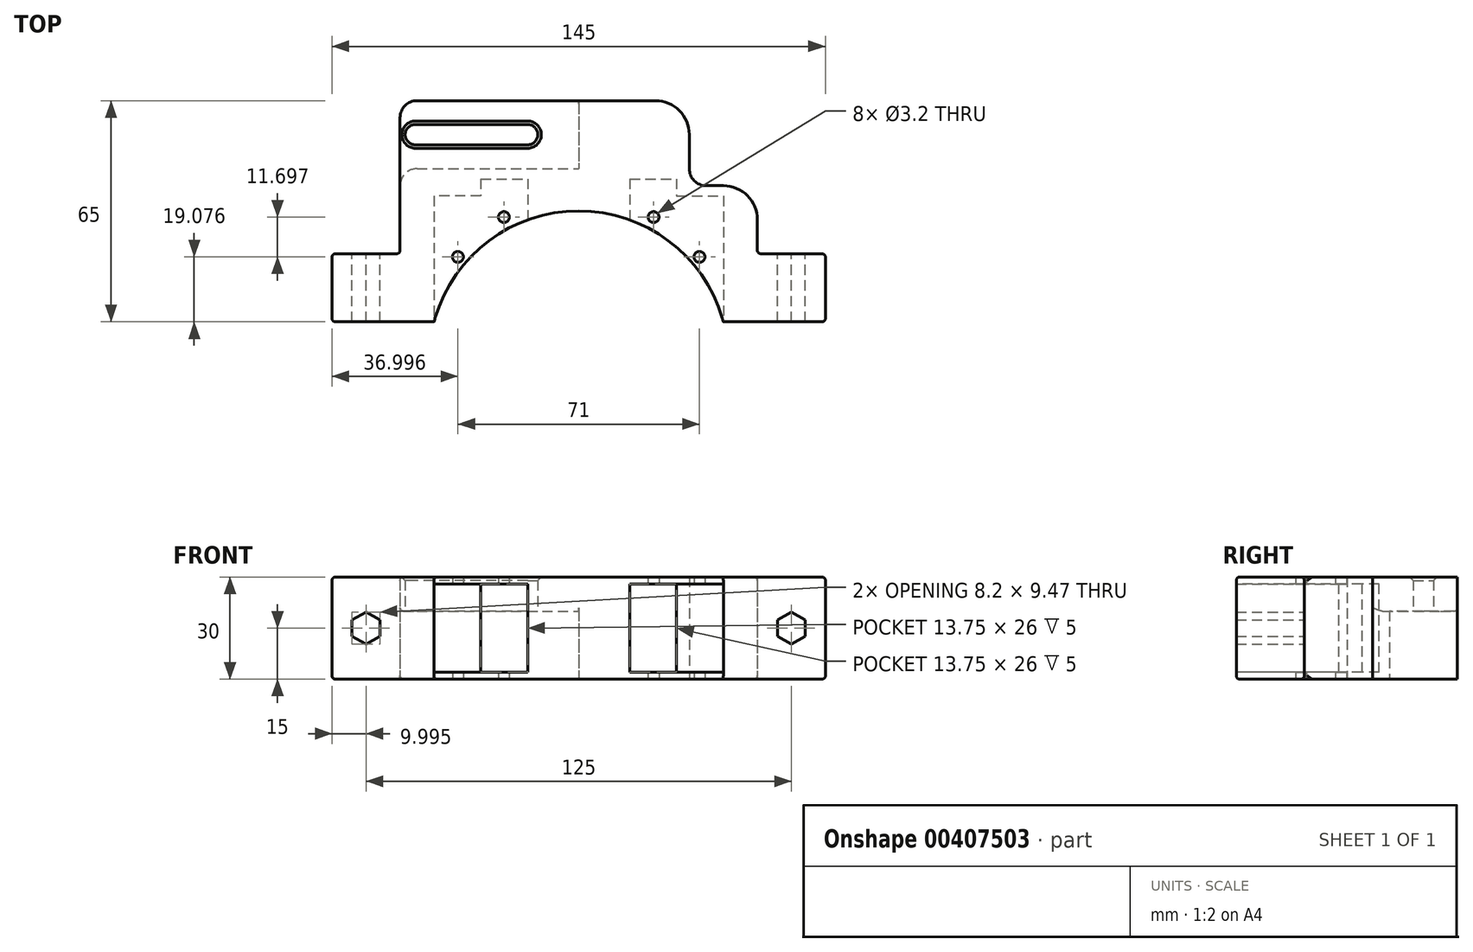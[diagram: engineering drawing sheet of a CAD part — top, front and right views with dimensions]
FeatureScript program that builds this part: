
annotation { "Feature Type Name" : "Feature", "Feature Type Description" : "" }
export const myFeature = defineFeature(function(context is Context, id is Id, definition is map)
    precondition{}
    {
        {
            var Q0;
            Q0=qCreatedBy(makeId("Top.planeOp"),FACE);
            var sketch = newSketch(context, id + "F0", { "sketchPlane" : qUnion([Q0])});
            skLineSegment(sketch, "E0", {"start": v(-52.77, 0.26) * mm, "end": v(-22.77, 0.26) * mm});
            skLineSegment(sketch, "E1", {"start": v(62.23, 0.26) * mm, "end": v(92.23, 0.26) * mm});
            skLineSegment(sketch, "E2", {"start": v(-52.77, 0.26) * mm, "end": v(-52.77, 20.26) * mm});
            skLineSegment(sketch, "E3", {"start": v(-52.77, 20.26) * mm, "end": v(-32.77, 20.26) * mm});
            skLineSegment(sketch, "E4", {"start": v(19.73, -73.35) * mm, "end": v(19.73, 79.15) * mm, "construction": true});
            skPoint(sketch, "E4.endSnap0", {"position": v(19.73, 11.65) * mm});
            skLineSegment(sketch, "E5", {"start": v(92.23, 0.26) * mm, "end": v(92.23, 20.26) * mm});
            skLineSegment(sketch, "E6", {"start": v(92.23, 20.26) * mm, "end": v(72.23, 20.26) * mm});
            skArc(sketch, "E7", {"start": v(62.23, 0.26) * mm, "mid": v(19.73, 32.87) * mm, "end": v(-22.77, 0.26) * mm});
            skLineSegment(sketch, "E8", {"start": v(-32.77, 20.26) * mm, "end": v(-32.77, 40.26) * mm});
            skLineSegment(sketch, "E9", {"start": v(-32.77, 40.26) * mm, "end": v(-12.77, 40.26) * mm});
            skLineSegment(sketch, "E10", {"start": v(-12.77, 40.26) * mm, "end": v(-12.77, 65.26) * mm});
            skLineSegment(sketch, "E11", {"start": v(72.23, 20.26) * mm, "end": v(72.23, 40.26) * mm});
            skLineSegment(sketch, "E12", {"start": v(72.23, 40.26) * mm, "end": v(52.23, 40.26) * mm});
            skLineSegment(sketch, "E13", {"start": v(52.23, 40.26) * mm, "end": v(52.23, 65.26) * mm});
            skLineSegment(sketch, "E14", {"start": v(-12.77, 65.26) * mm, "end": v(52.23, 65.26) * mm});
            skSolve(sketch);
        }
        {
            var Q0;
            Q0=makeQuery(id+"F0.imprint","IMPRINT",FACE,{"disambiguationData":[TD([[makeQuery(id+"F0.imprint","IMPRINT",EDGE,{"derivedFrom":sQuery(id+"F0.wireOp",EDGE,"E0")}),1.0]])]});
            extrude(context, id + "F1", {"entities" : qUnion([Q0]), "depth" : 30 * mm});
        }
        {
            var Q0;
            Q0=makeQuery(id+"F1.opExtrude","SWEPT_FACE",FACE,{"disambiguationData":[OSD([sQuery(id+"F0.wireOp",EDGE,"E0")])]});
            cPlane(context, id + "F2", {"entities" : qUnion([Q0]), "cplaneType" : CPlaneType.OFFSET, "offset" : 0 * mm, "width" : 150 * mm, "height" : 150 * mm});
        }
        {
            var Q0;
            Q0=qCreatedBy(id+"F2.planeOp",FACE);
            var sketch = newSketch(context, id + "F3", { "sketchPlane" : qUnion([Q0])});
            skLineSegment(sketch, "E15", {"start": v(-22.77, 28) * mm, "end": v(4.73, 28) * mm});
            skLineSegment(sketch, "E16", {"start": v(4.73, 28) * mm, "end": v(4.73, 2) * mm});
            skLineSegment(sketch, "E17", {"start": v(4.73, 2) * mm, "end": v(-22.77, 2) * mm});
            skLineSegment(sketch, "E18", {"start": v(-22.77, 2) * mm, "end": v(-22.77, 28) * mm});
            skLineSegment(sketch, "E19", {"start": v(34.73, 28) * mm, "end": v(62.23, 28) * mm});
            skLineSegment(sketch, "E20", {"start": v(62.23, 28) * mm, "end": v(62.23, 2) * mm});
            skLineSegment(sketch, "E21", {"start": v(62.23, 2) * mm, "end": v(34.73, 2) * mm});
            skLineSegment(sketch, "E22", {"start": v(34.73, 2) * mm, "end": v(34.73, 28) * mm});
            skSolve(sketch);
        }
        {
            var Q0;
            Q0=makeQuery(id+"F3.imprint","IMPRINT",FACE,{"disambiguationData":[TD([[makeQuery(id+"F3.imprint","IMPRINT",EDGE,{"derivedFrom":sQuery(id+"F3.wireOp",EDGE,"E15")}),-1.0]])]});
            var Q1;
            Q1=makeQuery(id+"F3.imprint","IMPRINT",FACE,{"disambiguationData":[TD([[makeQuery(id+"F3.imprint","IMPRINT",EDGE,{"derivedFrom":sQuery(id+"F3.wireOp",EDGE,"E19")}),-1.0]])]});
            extrude(context, id + "F4", {"entities" : qUnion([Q0, Q1]), "operationType" : NewBodyOperationType.REMOVE, "oppositeDirection" : true, "depth" : 37 * mm});
        }
        {
            var Q0;
            Q0=makeQuery(id+"F1.opExtrude","SWEPT_FACE",FACE,{"disambiguationData":[OSD([sQuery(id+"F0.wireOp",EDGE,"E3")])]});
            var sketch = newSketch(context, id + "F5", { "sketchPlane" : qUnion([Q0])});
            skCircle(sketch, "E23.cCircle", {"center": v(42.77, 15) * mm, "radius": 4.1 * mm, "construction": true});
            skPoint(sketch, "E23.cCircle.centerSnap0", {"position": v(52.77, 15) * mm});
            skLineSegment(sketch, "E23.0", {"start": v(46.87, 12.63) * mm, "end": v(42.77, 10.27) * mm});
            skLineSegment(sketch, "E23.1", {"start": v(42.77, 10.27) * mm, "end": v(38.67, 12.63) * mm});
            skLineSegment(sketch, "E23.2", {"start": v(38.67, 12.63) * mm, "end": v(38.67, 17.37) * mm});
            skLineSegment(sketch, "E23.3", {"start": v(38.67, 17.37) * mm, "end": v(42.77, 19.73) * mm});
            skLineSegment(sketch, "E23.4", {"start": v(42.77, 19.73) * mm, "end": v(46.87, 17.37) * mm});
            skLineSegment(sketch, "E23.5", {"start": v(46.87, 17.37) * mm, "end": v(46.87, 12.63) * mm});
            skPoint(sketch, "E23.0.midPoint", {"position": v(44.82, 11.45) * mm});
            skSolve(sketch);
        }
        {
            var Q0;
            Q0=makeQuery(id+"F1.opExtrude","SWEPT_FACE",FACE,{"disambiguationData":[OSD([sQuery(id+"F0.wireOp",EDGE,"E6")])]});
            var sketch = newSketch(context, id + "F6", { "sketchPlane" : qUnion([Q0])});
            skCircle(sketch, "E24.cCircle", {"center": v(-82.23, 15) * mm, "radius": 4.1 * mm, "construction": true});
            skLineSegment(sketch, "E24.0", {"start": v(-86.33, 12.63) * mm, "end": v(-86.33, 17.37) * mm});
            skLineSegment(sketch, "E24.1", {"start": v(-86.33, 17.37) * mm, "end": v(-82.23, 19.73) * mm});
            skLineSegment(sketch, "E24.2", {"start": v(-82.23, 19.73) * mm, "end": v(-78.13, 17.37) * mm});
            skLineSegment(sketch, "E24.3", {"start": v(-78.13, 17.37) * mm, "end": v(-78.13, 12.63) * mm});
            skLineSegment(sketch, "E24.4", {"start": v(-78.13, 12.63) * mm, "end": v(-82.23, 10.27) * mm});
            skLineSegment(sketch, "E24.5", {"start": v(-82.23, 10.27) * mm, "end": v(-86.33, 12.63) * mm});
            skPoint(sketch, "E24.0.midPoint", {"position": v(-86.33, 15) * mm});
            skSolve(sketch);
        }
        {
            var Q0;
            Q0=qSketchRegion(id+"F6",true);
            var Q1;
            Q1=qSketchRegion(id+"F5",true);
            extrude(context, id + "F7", {"entities" : qUnion([Q0, Q1]), "operationType" : NewBodyOperationType.REMOVE, "endBound" : BoundingType.THROUGH_ALL, "oppositeDirection" : true, "depth" : 25 * mm});
        }
        {
            var Q0;
            Q0=makeQuery(id+"F4.boolean.opBoolean","COPY",FACE,{"derivedFrom":makeQuery(id+"F4.opExtrude","SWEPT_FACE",FACE,{"disambiguationData":[OSD([sQuery(id+"F3.wireOp",EDGE,"E19")])]})});
            var sketch = newSketch(context, id + "F8", { "sketchPlane" : qUnion([Q0])});
            skArc(sketch, "E25", {"start": v(34.73, -34.23) * mm, "mid": v(51.68, -23.4) * mm, "end": v(62.23, -6.26) * mm, "construction": true});
            skCircle(sketch, "E26", {"center": v(55.23, -19.34) * mm, "radius": 1.6 * mm});
            skCircle(sketch, "E27", {"center": v(41.73, -31.03) * mm, "radius": 1.6 * mm});
            skLineSegment(sketch, "E28", {"start": v(19.73, -44) * mm, "end": v(19.73, 3.8) * mm, "construction": true});
            skCircle(sketch, "E29.MirrorC", {"center": v(-15.77, -19.34) * mm, "radius": 1.6 * mm});
            skCircle(sketch, "E30.MirrorC", {"center": v(-2.27, -31.03) * mm, "radius": 1.6 * mm});
            skSolve(sketch);
        }
        {
            var Q0;
            Q0=makeQuery(id+"F4.boolean.opBoolean","COPY",FACE,{"derivedFrom":makeQuery(id+"F4.opExtrude","CAP_FACE",FACE,{"disambiguationData":[OSD([sQuery(id+"F3.wireOp",EDGE,"E19"),sQuery(id+"F3.wireOp",EDGE,"E20"),sQuery(id+"F3.wireOp",EDGE,"E21"),sQuery(id+"F3.wireOp",EDGE,"E22")])],"isStart":false})});
            var sketch = newSketch(context, id + "F9", { "sketchPlane" : qUnion([Q0])});
            skLineSegment(sketch, "E31.bottom", {"start": v(48.48, 2) * mm, "end": v(34.73, 2) * mm});
            skLineSegment(sketch, "E31.top", {"start": v(48.48, 28) * mm, "end": v(34.73, 28) * mm});
            skLineSegment(sketch, "E31.left", {"start": v(48.48, 2) * mm, "end": v(48.48, 28) * mm});
            skLineSegment(sketch, "E31.right", {"start": v(34.73, 2) * mm, "end": v(34.73, 28) * mm});
            skSolve(sketch);
        }
        {
            var Q0;
            Q0=makeQuery(id+"F4.boolean.opBoolean","COPY",FACE,{"derivedFrom":makeQuery(id+"F4.opExtrude","CAP_FACE",FACE,{"disambiguationData":[OSD([sQuery(id+"F3.wireOp",EDGE,"E15"),sQuery(id+"F3.wireOp",EDGE,"E16"),sQuery(id+"F3.wireOp",EDGE,"E17"),sQuery(id+"F3.wireOp",EDGE,"E18")])],"isStart":false})});
            var sketch = newSketch(context, id + "F10", { "sketchPlane" : qUnion([Q0])});
            skLineSegment(sketch, "E32.bottom", {"start": v(-9.02, 2) * mm, "end": v(4.73, 2) * mm});
            skLineSegment(sketch, "E32.top", {"start": v(-9.02, 28) * mm, "end": v(4.73, 28) * mm});
            skLineSegment(sketch, "E32.left", {"start": v(-9.02, 2) * mm, "end": v(-9.02, 28) * mm});
            skLineSegment(sketch, "E32.right", {"start": v(4.73, 2) * mm, "end": v(4.73, 28) * mm});
            skSolve(sketch);
        }
        {
            var Q0;
            Q0=makeQuery(id+"F9.imprint","IMPRINT",FACE,{"disambiguationData":[TD([[makeQuery(id+"F9.imprint","IMPRINT",EDGE,{"derivedFrom":sQuery(id+"F9.wireOp",EDGE,"E31.bottom")}),-1.0]])]});
            var Q1;
            Q1=qSketchRegion(id+"F10",true);
            extrude(context, id + "F11", {"entities" : qUnion([Q0, Q1]), "operationType" : NewBodyOperationType.REMOVE, "oppositeDirection" : true, "depth" : 5 * mm});
        }
        {
            var Q0;
            Q0=qSketchRegion(id+"F8",true);
            extrude(context, id + "F12", {"entities" : qUnion([Q0]), "operationType" : NewBodyOperationType.REMOVE, "endBound" : BoundingType.THROUGH_ALL, "oppositeDirection" : true, "depth" : 25 * mm, "hasSecondDirection" : true, "secondDirectionBound" : SecondDirectionBoundingType.THROUGH_ALL, "secondDirectionOppositeDirection" : false, "secondDirectionDepth" : 25 * mm});
        }
        {
            var Q0;
            Q0=makeQuery(id+"F1.opExtrude","CAP_FACE",FACE,{"disambiguationData":[OSD([sQuery(id+"F0.wireOp",EDGE,"E0"),sQuery(id+"F0.wireOp",EDGE,"E1"),sQuery(id+"F0.wireOp",EDGE,"E2"),sQuery(id+"F0.wireOp",EDGE,"E3"),sQuery(id+"F0.wireOp",EDGE,"E5"),sQuery(id+"F0.wireOp",EDGE,"E6"),sQuery(id+"F0.wireOp",EDGE,"E7"),sQuery(id+"F0.wireOp",EDGE,"E8"),sQuery(id+"F0.wireOp",EDGE,"E9"),sQuery(id+"F0.wireOp",EDGE,"E10"),sQuery(id+"F0.wireOp",EDGE,"E11"),sQuery(id+"F0.wireOp",EDGE,"E12"),sQuery(id+"F0.wireOp",EDGE,"E13"),sQuery(id+"F0.wireOp",EDGE,"E14")])],"isStart":true});
            var sketch = newSketch(context, id + "F13", { "sketchPlane" : qUnion([Q0])});
            skLineSegment(sketch, "E33.bottom", {"start": v(-12.77, -65.26) * mm, "end": v(19.73, -65.26) * mm});
            skLineSegment(sketch, "E33.top", {"start": v(-12.77, -45.26) * mm, "end": v(19.73, -45.26) * mm});
            skLineSegment(sketch, "E33.left", {"start": v(-12.77, -65.26) * mm, "end": v(-12.77, -45.26) * mm});
            skLineSegment(sketch, "E33.right", {"start": v(19.73, -65.26) * mm, "end": v(19.73, -45.26) * mm});
            skSolve(sketch);
        }
        {
            var Q0;
            Q0 = qSketchRegion(id + "F13", true);
            extrude(context, id + "F14", {"entities" : qUnion([Q0]), "operationType" : NewBodyOperationType.REMOVE, "oppositeDirection" : true, "depth" : 20 * mm});
        }
        {
            var Q0;
            Q0=makeQuery(id+"F1.opExtrude","SWEPT_FACE",FACE,{"disambiguationData":[OSD([sQuery(id+"F0.wireOp",EDGE,"E10")])]});
            var Q1;
            Q1=makeQuery(id+"F1.opExtrude","SWEPT_FACE",FACE,{"disambiguationData":[OSD([sQuery(id+"F0.wireOp",EDGE,"E8")])]});
            extrude(context, id + "F15", {"entities" : qUnion([Q0]), "operationType" : NewBodyOperationType.ADD, "endBound" : BoundingType.UP_TO_SURFACE, "endBoundEntityFace" : qUnion([Q1]), "depth" : 25 * mm});
        }
        {
            var Q0;
            {var subQ0=sQuery(id+"F13.wireOp",EDGE,"E33.left");Q0=makeQuery(id+"F15.boolean.opBoolean","MERGE",FACE,{"derivedFrom":[makeQuery(id+"F14.boolean.opBoolean","COPY",FACE,{"derivedFrom":makeQuery(id+"F14.opExtrude","CAP_FACE",FACE,{"disambiguationData":[OSD([sQuery(id+"F13.wireOp",EDGE,"E33.bottom"),sQuery(id+"F13.wireOp",EDGE,"E33.top"),subQ0,sQuery(id+"F13.wireOp",EDGE,"E33.right")])],"isStart":false})}),makeQuery(id+"F15.opExtrude","SWEPT_FACE",FACE,{"disambiguationData":[OSD([subQ0])]})]});}
            var sketch = newSketch(context, id + "F16", { "sketchPlane" : qUnion([Q0])});
            skLineSegment(sketch, "E34", {"start": v(19.73, -55.26) * mm, "end": v(-32.77, -55.26) * mm, "construction": true});
            skLineSegment(sketch, "E35", {"start": v(4.73, -58.26) * mm, "end": v(-28.27, -58.26) * mm});
            skLineSegment(sketch, "E36", {"start": v(4.73, -52.26) * mm, "end": v(-28.27, -52.26) * mm});
            skArc(sketch, "E37", {"start": v(4.73, -58.26) * mm, "mid": v(7.73, -55.26) * mm, "end": v(4.73, -52.26) * mm});
            skArc(sketch, "E38", {"start": v(-28.27, -52.26) * mm, "mid": v(-31.27, -55.26) * mm, "end": v(-28.27, -58.26) * mm});
            skSolve(sketch);
        }
        {
            var Q0;
            Q0=makeQuery(id+"F16.imprint","IMPRINT",FACE,{"disambiguationData":[TD([[makeQuery(id+"F16.imprint","IMPRINT",EDGE,{"derivedFrom":sQuery(id+"F16.wireOp",EDGE,"E35")}),-1.0]])]});
            extrude(context, id + "F17", {"entities" : qUnion([Q0]), "operationType" : NewBodyOperationType.REMOVE, "endBound" : BoundingType.THROUGH_ALL, "oppositeDirection" : true, "depth" : 25 * mm});
        }
        {
            var Q0;
            Q0=makeQuery(id+"F1.opExtrude","SWEPT_EDGE",EDGE,{"disambiguationData":[OSD([sQuery(id+"F0.wireOp",EDGE,"E13"),sQuery(id+"F0.wireOp",EDGE,"E14")])]});
            var Q1;
            Q1=makeQuery(id+"F1.opExtrude","SWEPT_EDGE",EDGE,{"disambiguationData":[OSD([sQuery(id+"F0.wireOp",EDGE,"E11"),sQuery(id+"F0.wireOp",EDGE,"E12")])]});
            fillet(context, id + "F18", {"entities" : qUnion([Q0, Q1]), "radius" : 10 * mm, "tangentPropagation" : true, "allowEdgeOverflow" : false});
        }
        {
            var Q0;
            Q0=makeQuery(id+"F1.opExtrude","SWEPT_EDGE",EDGE,{"disambiguationData":[OSD([sQuery(id+"F0.wireOp",EDGE,"E12"),sQuery(id+"F0.wireOp",EDGE,"E13")])]});
            var Q1;
            Q1=makeQuery(id+"F15.opExtrude","CAP_EDGE",EDGE,{"disambiguationData":[OSD([sQuery(id+"F0.wireOp",EDGE,"E10"),sQuery(id+"F0.wireOp",EDGE,"E14")])],"isStart":false});
            var Q2;
            Q2=makeQuery(id+"F15.opExtrude","CAP_EDGE",EDGE,{"disambiguationData":[OSD([sQuery(id+"F0.wireOp",EDGE,"E10"),sQuery(id+"F13.wireOp",EDGE,"E33.top"),sQuery(id+"F13.wireOp",EDGE,"E33.left")])],"isStart":false});
            fillet(context, id + "F19", {"entities" : qUnion([Q0, Q1, Q2]), "radius" : 5 * mm, "tangentPropagation" : true, "allowEdgeOverflow" : false});
        }
        {
            var Q0;
            Q0=makeQuery(id+"F1.opExtrude","CAP_EDGE",EDGE,{"disambiguationData":[OSD([sQuery(id+"F0.wireOp",EDGE,"E6")])],"isStart":false});
            var Q1;
            Q1=makeQuery(id+"F1.opExtrude","CAP_EDGE",EDGE,{"disambiguationData":[OSD([sQuery(id+"F0.wireOp",EDGE,"E5")])],"isStart":false});
            var Q2;
            Q2=makeQuery(id+"F1.opExtrude","CAP_EDGE",EDGE,{"disambiguationData":[OSD([sQuery(id+"F0.wireOp",EDGE,"E1")])],"isStart":false});
            var Q3;
            Q3=makeQuery(id+"F1.opExtrude","SWEPT_EDGE",EDGE,{"disambiguationData":[OSD([sQuery(id+"F0.wireOp",EDGE,"E1"),sQuery(id+"F0.wireOp",EDGE,"E5")])]});
            var Q4;
            Q4=makeQuery(id+"F1.opExtrude","CAP_EDGE",EDGE,{"disambiguationData":[OSD([sQuery(id+"F0.wireOp",EDGE,"E1")])],"isStart":true});
            var Q5;
            Q5=makeQuery(id+"F1.opExtrude","CAP_EDGE",EDGE,{"disambiguationData":[OSD([sQuery(id+"F0.wireOp",EDGE,"E5")])],"isStart":true});
            var Q6;
            Q6=makeQuery(id+"F1.opExtrude","CAP_EDGE",EDGE,{"disambiguationData":[OSD([sQuery(id+"F0.wireOp",EDGE,"E6")])],"isStart":true});
            var Q7;
            Q7=makeQuery(id+"F1.opExtrude","SWEPT_EDGE",EDGE,{"disambiguationData":[OSD([sQuery(id+"F0.wireOp",EDGE,"E5"),sQuery(id+"F0.wireOp",EDGE,"E6")])]});
            var Q8;
            Q8=makeQuery(id+"F1.opExtrude","SWEPT_EDGE",EDGE,{"disambiguationData":[OSD([sQuery(id+"F0.wireOp",EDGE,"E6"),sQuery(id+"F0.wireOp",EDGE,"E11")])]});
            var Q9;
            Q9=makeQuery(id+"F1.opExtrude","CAP_EDGE",EDGE,{"disambiguationData":[OSD([sQuery(id+"F0.wireOp",EDGE,"E3")])],"isStart":false});
            var Q10;
            Q10=makeQuery(id+"F1.opExtrude","CAP_EDGE",EDGE,{"disambiguationData":[OSD([sQuery(id+"F0.wireOp",EDGE,"E0")])],"isStart":false});
            var Q11;
            Q11=makeQuery(id+"F1.opExtrude","CAP_EDGE",EDGE,{"disambiguationData":[OSD([sQuery(id+"F0.wireOp",EDGE,"E2")])],"isStart":false});
            var Q12;
            Q12=makeQuery(id+"F1.opExtrude","SWEPT_EDGE",EDGE,{"disambiguationData":[OSD([sQuery(id+"F0.wireOp",EDGE,"E2"),sQuery(id+"F0.wireOp",EDGE,"E3")])]});
            var Q13;
            Q13=makeQuery(id+"F1.opExtrude","SWEPT_EDGE",EDGE,{"disambiguationData":[OSD([sQuery(id+"F0.wireOp",EDGE,"E0"),sQuery(id+"F0.wireOp",EDGE,"E2")])]});
            var Q14;
            Q14=makeQuery(id+"F1.opExtrude","CAP_EDGE",EDGE,{"disambiguationData":[OSD([sQuery(id+"F0.wireOp",EDGE,"E0")])],"isStart":true});
            var Q15;
            Q15=makeQuery(id+"F1.opExtrude","CAP_EDGE",EDGE,{"disambiguationData":[OSD([sQuery(id+"F0.wireOp",EDGE,"E2")])],"isStart":true});
            var Q16;
            Q16=makeQuery(id+"F1.opExtrude","CAP_EDGE",EDGE,{"disambiguationData":[OSD([sQuery(id+"F0.wireOp",EDGE,"E3")])],"isStart":true});
            var Q17;
            Q17=makeQuery(id+"F1.opExtrude","SWEPT_EDGE",EDGE,{"disambiguationData":[OSD([sQuery(id+"F0.wireOp",EDGE,"E3"),sQuery(id+"F0.wireOp",EDGE,"E8")])]});
            var Q18;
            Q18=makeQuery(id+"F14.boolean.opBoolean","COPY",EDGE,{"derivedFrom":makeQuery(id+"F14.opExtrude","CAP_EDGE",EDGE,{"disambiguationData":[OSD([sQuery(id+"F13.wireOp",EDGE,"E33.right")])],"isStart":true})});
            var Q19;
            Q19=makeQuery(id+"F14.boolean.opBoolean","COPY",EDGE,{"derivedFrom":makeQuery(id+"F14.opExtrude","SWEPT_EDGE",EDGE,{"disambiguationData":[OSD([sQuery(id+"F0.wireOp",EDGE,"E14"),sQuery(id+"F13.wireOp",EDGE,"E33.bottom"),sQuery(id+"F13.wireOp",EDGE,"E33.right")])]})});
            var Q20;
            {var subQ0=sQuery(id+"F13.wireOp",EDGE,"E33.bottom");Q20=makeQuery(id+"F15.boolean.opBoolean","MERGE",EDGE,{"derivedFrom":[makeQuery(id+"F14.boolean.opBoolean","COPY",EDGE,{"derivedFrom":makeQuery(id+"F14.opExtrude","CAP_EDGE",EDGE,{"disambiguationData":[OSD([subQ0])],"isStart":false})}),makeQuery(id+"F15.opExtrude","SWEPT_EDGE",EDGE,{"disambiguationData":[OSD([subQ0,sQuery(id+"F13.wireOp",EDGE,"E33.left")])]})]});}
            fillet(context, id + "F20", {"entities" : qUnion([Q0, Q1, Q2, Q3, Q4, Q5, Q6, Q7, Q8, Q9, Q10, Q11, Q12, Q13, Q14, Q15, Q16, Q17, Q18, Q19, Q20]), "radius" : 1 * mm, "tangentPropagation" : true, "allowEdgeOverflow" : false});
        }
        {
            var Q0;
            Q0=makeQuery(id+"F17.boolean.opBoolean","COPY",EDGE,{"derivedFrom":makeQuery(id+"F17.opExtrude","CAP_EDGE",EDGE,{"disambiguationData":[OSD([sQuery(id+"F16.wireOp",EDGE,"E35")])],"isStart":true})});
            var Q1;
            Q1=makeQuery(id+"F17.boolean.opBoolean","COPY",EDGE,{"derivedFrom":makeQuery(id+"F17.opExtrude","CAP_EDGE",EDGE,{"disambiguationData":[OSD([sQuery(id+"F16.wireOp",EDGE,"E37")])],"isStart":true})});
            var Q2;
            Q2=makeQuery(id+"F17.boolean.opBoolean","COPY",EDGE,{"derivedFrom":makeQuery(id+"F17.opExtrude","CAP_EDGE",EDGE,{"disambiguationData":[OSD([sQuery(id+"F16.wireOp",EDGE,"E36")])],"isStart":true})});
            var Q3;
            Q3=makeQuery(id+"F17.boolean.opBoolean","COPY",EDGE,{"derivedFrom":makeQuery(id+"F17.opExtrude","CAP_EDGE",EDGE,{"disambiguationData":[OSD([sQuery(id+"F16.wireOp",EDGE,"E38")])],"isStart":true})});
            var Q4;
            {var subQ0=sQuery(id+"F0.wireOp",EDGE,"E10");Q4=makeQuery(id+"F17.boolean.opBoolean","INTERSECT",EDGE,{"derivedFrom":[makeQuery(id+"F15.boolean.opBoolean","MERGE",FACE,{"derivedFrom":[makeQuery(id+"F1.opExtrude","CAP_FACE",FACE,{"disambiguationData":[OSD([sQuery(id+"F0.wireOp",EDGE,"E0"),sQuery(id+"F0.wireOp",EDGE,"E1"),sQuery(id+"F0.wireOp",EDGE,"E2"),sQuery(id+"F0.wireOp",EDGE,"E3"),sQuery(id+"F0.wireOp",EDGE,"E5"),sQuery(id+"F0.wireOp",EDGE,"E6"),sQuery(id+"F0.wireOp",EDGE,"E7"),sQuery(id+"F0.wireOp",EDGE,"E8"),sQuery(id+"F0.wireOp",EDGE,"E9"),subQ0,sQuery(id+"F0.wireOp",EDGE,"E11"),sQuery(id+"F0.wireOp",EDGE,"E12"),sQuery(id+"F0.wireOp",EDGE,"E13"),sQuery(id+"F0.wireOp",EDGE,"E14")])],"isStart":false}),makeQuery(id+"F15.opExtrude","SWEPT_FACE",FACE,{"disambiguationData":[OSD([subQ0]),TDD([makeQuery(id+"F1.opExtrude","CAP_EDGE",EDGE,{"disambiguationData":[OSD([subQ0])],"isStart":false})])]})]}),makeQuery(id+"F17.opExtrude","SWEPT_FACE",FACE,{"disambiguationData":[OSD([sQuery(id+"F16.wireOp",EDGE,"E35")])]})]});}
            chamfer(context, id + "F21", {"entities" : qUnion([Q0, Q1, Q2, Q3, Q4]), "width" : 1 * mm, "tangentPropagation" : true});
        }
    });
